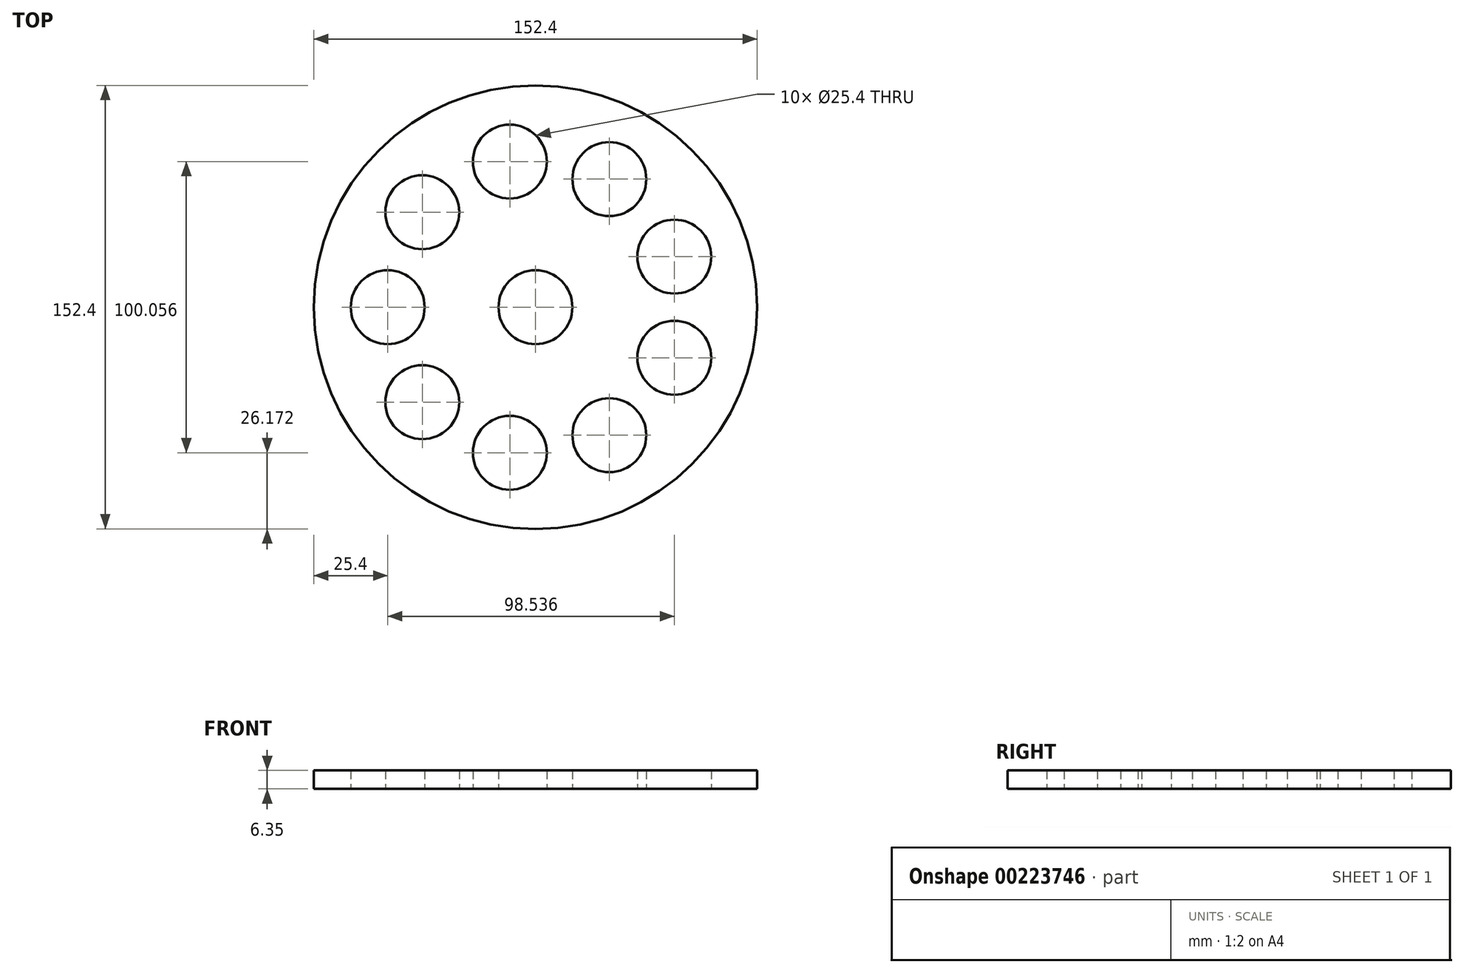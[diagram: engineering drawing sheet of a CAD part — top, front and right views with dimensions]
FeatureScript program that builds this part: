
annotation { "Feature Type Name" : "Feature", "Feature Type Description" : "" }
export const myFeature = defineFeature(function(context is Context, id is Id, definition is map)
    precondition{}
    {
        {
            var Q0;
            Q0=qCreatedBy(makeId("Top.planeOp"),FACE);
            var sketch = newSketch(context, id + "F0", { "sketchPlane" : qUnion([Q0])});
            skCircle(sketch, "E0", {"center": v(0, 0) * mm, "radius": 76.2 * mm});
            skCircle(sketch, "E1", {"center": v(0, 0) * mm, "radius": 12.7 * mm});
            skLineSegment(sketch, "E2", {"start": v(0, 0) * mm, "end": v(-76.2, 0) * mm, "construction": true});
            skLineSegment(sketch, "E3", {"start": v(-76.2, 0) * mm, "end": v(-50.8, 0) * mm, "construction": true});
            skCircle(sketch, "E4", {"center": v(-50.8, 0) * mm, "radius": 12.7 * mm});
            skCircle(sketch, "E5.1.0", {"center": v(-38.92, -32.65) * mm, "radius": 12.7 * mm});
            skCircle(sketch, "E5.2.0", {"center": v(-8.82, -50.03) * mm, "radius": 12.7 * mm});
            skCircle(sketch, "E5.3.0", {"center": v(25.4, -44) * mm, "radius": 12.7 * mm});
            skCircle(sketch, "E5.4.0", {"center": v(47.74, -17.37) * mm, "radius": 12.7 * mm});
            skCircle(sketch, "E5.5.0", {"center": v(47.74, 17.37) * mm, "radius": 12.7 * mm});
            skCircle(sketch, "E5.6.0", {"center": v(25.4, 44) * mm, "radius": 12.7 * mm});
            skCircle(sketch, "E5.7.0", {"center": v(-8.82, 50.03) * mm, "radius": 12.7 * mm});
            skCircle(sketch, "E5.8.0", {"center": v(-38.92, 32.65) * mm, "radius": 12.7 * mm});
            skSolve(sketch);
        }
        {
            var Q0;
            Q0 = qSketchRegion(id + "F0", true);
            extrude(context, id + "F1", {"entities" : qUnion([Q0]), "depth" : 6.35 * mm});
        }
    });
